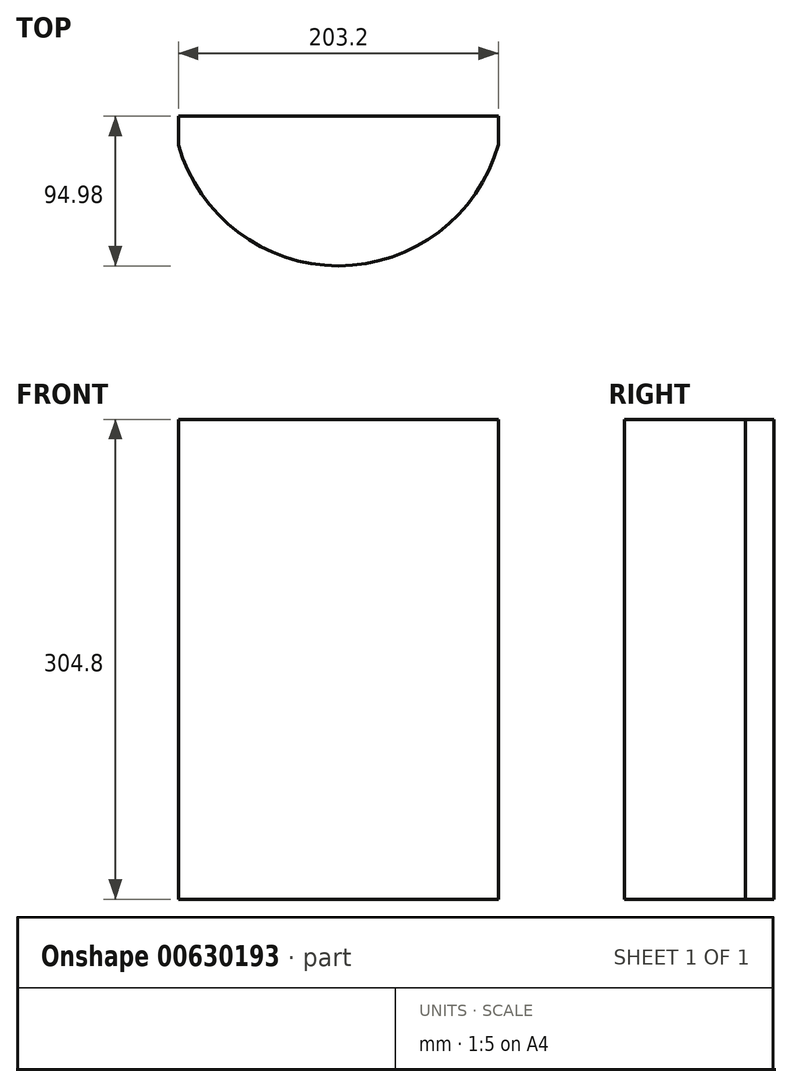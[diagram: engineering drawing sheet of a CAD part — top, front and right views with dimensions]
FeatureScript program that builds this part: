
annotation { "Feature Type Name" : "Feature", "Feature Type Description" : "" }
export const myFeature = defineFeature(function(context is Context, id is Id, definition is map)
    precondition{}
    {
        {
            var Q0;
            Q0=qCreatedBy(makeId("Front.planeOp"),FACE);
            var sketch = newSketch(context, id + "F0", { "sketchPlane" : qUnion([Q0])});
            skLineSegment(sketch, "E0.bottom", {"start": v(-101.6, 152.4) * mm, "end": v(101.6, 152.4) * mm});
            skLineSegment(sketch, "E0.top", {"start": v(-101.6, -152.4) * mm, "end": v(101.6, -152.4) * mm});
            skLineSegment(sketch, "E0.left", {"start": v(-101.6, 152.4) * mm, "end": v(-101.6, -152.4) * mm});
            skLineSegment(sketch, "E0.right", {"start": v(101.6, 152.4) * mm, "end": v(101.6, -152.4) * mm});
            skPoint(sketch, "E0.middle", {"position": v(0, 0) * mm});
            skSolve(sketch);
        }
        {
            var Q0;
            Q0 = qSketchRegion(id + "F0", true);
            extrude(context, id + "F1", {"entities" : qUnion([Q0]), "depth" : 95.25 * mm, "offsetDistance" : 25.4 * mm});
        }
        {
            var Q0;
            Q0=makeQuery(id+"F1.opExtrude","SWEPT_FACE",FACE,{"disambiguationData":[OSD([sQuery(id+"F0.wireOp",EDGE,"E0.bottom")])]});
            var sketch = newSketch(context, id + "F2", { "sketchPlane" : qUnion([Q0])});
            skArc(sketch, "E1", {"start": v(-101.6, -18.17) * mm, "mid": v(0.1, -94.98) * mm, "end": v(101.6, -17.9) * mm});
            skSolve(sketch);
        }
        {
            var Q0;
            {var subQ0=sQuery(id+"F2.wireOp",EDGE,"E1");Q0=makeQuery(id+"F2.imprint","IMPRINT",FACE,{"disambiguationData":[TD([[makeQuery(id+"F2.imprint","IMPRINT",EDGE,{"derivedFrom":subQ0}),-1.0]])]});}
            extrude(context, id + "F3", {"entities" : qUnion([Q0]), "operationType" : NewBodyOperationType.REMOVE, "oppositeDirection" : true, "depth" : 317.5 * mm, "offsetDistance" : 25.4 * mm});
        }
    });
